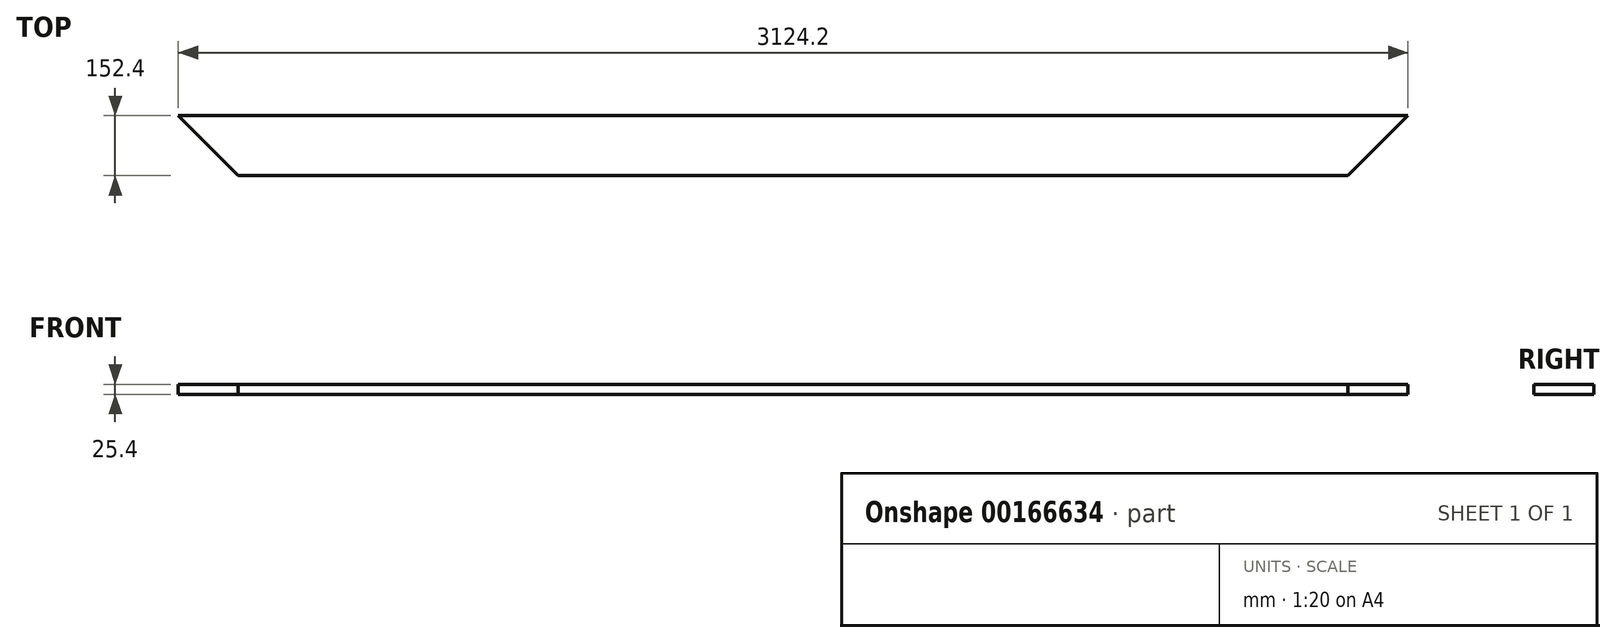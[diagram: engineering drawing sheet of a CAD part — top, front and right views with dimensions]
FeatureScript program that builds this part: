
annotation { "Feature Type Name" : "Feature", "Feature Type Description" : "" }
export const myFeature = defineFeature(function(context is Context, id is Id, definition is map)
    precondition{}
    {
        {
            var Q0;
            Q0=qCreatedBy(makeId("Top.planeOp"),FACE);
            var sketch = newSketch(context, id + "F0", { "sketchPlane" : qUnion([Q0])});
            skLineSegment(sketch, "E0.bottom", {"start": v(0, 0) * mm, "end": v(3124.2, 0) * mm});
            skLineSegment(sketch, "E0.top", {"start": v(0, -152.4) * mm, "end": v(3124.2, -152.4) * mm});
            skLineSegment(sketch, "E0.left", {"start": v(0, 0) * mm, "end": v(0, -152.4) * mm});
            skLineSegment(sketch, "E0.right", {"start": v(3124.2, 0) * mm, "end": v(3124.2, -152.4) * mm});
            skSolve(sketch);
        }
        {
            var Q0;
            Q0 = qSketchRegion(id + "F0", true);
            extrude(context, id + "F1", {"entities" : qUnion([Q0]), "depth" : 25.4 * mm});
        }
        {
            var Q0;
            Q0=makeQuery(id+"F1.opExtrude","SWEPT_EDGE",EDGE,{"disambiguationData":[OSD([sQuery(id+"F0.wireOp",EDGE,"E0.top"),sQuery(id+"F0.wireOp",EDGE,"E0.left")])]});
            var Q1;
            Q1=makeQuery(id+"F1.opExtrude","SWEPT_EDGE",EDGE,{"disambiguationData":[OSD([sQuery(id+"F0.wireOp",EDGE,"E0.top"),sQuery(id+"F0.wireOp",EDGE,"E0.right")])]});
            chamfer(context, id + "F2", {"entities" : qUnion([Q0, Q1]), "width" : 152.4 * mm, "tangentPropagation" : true});
        }
    });
